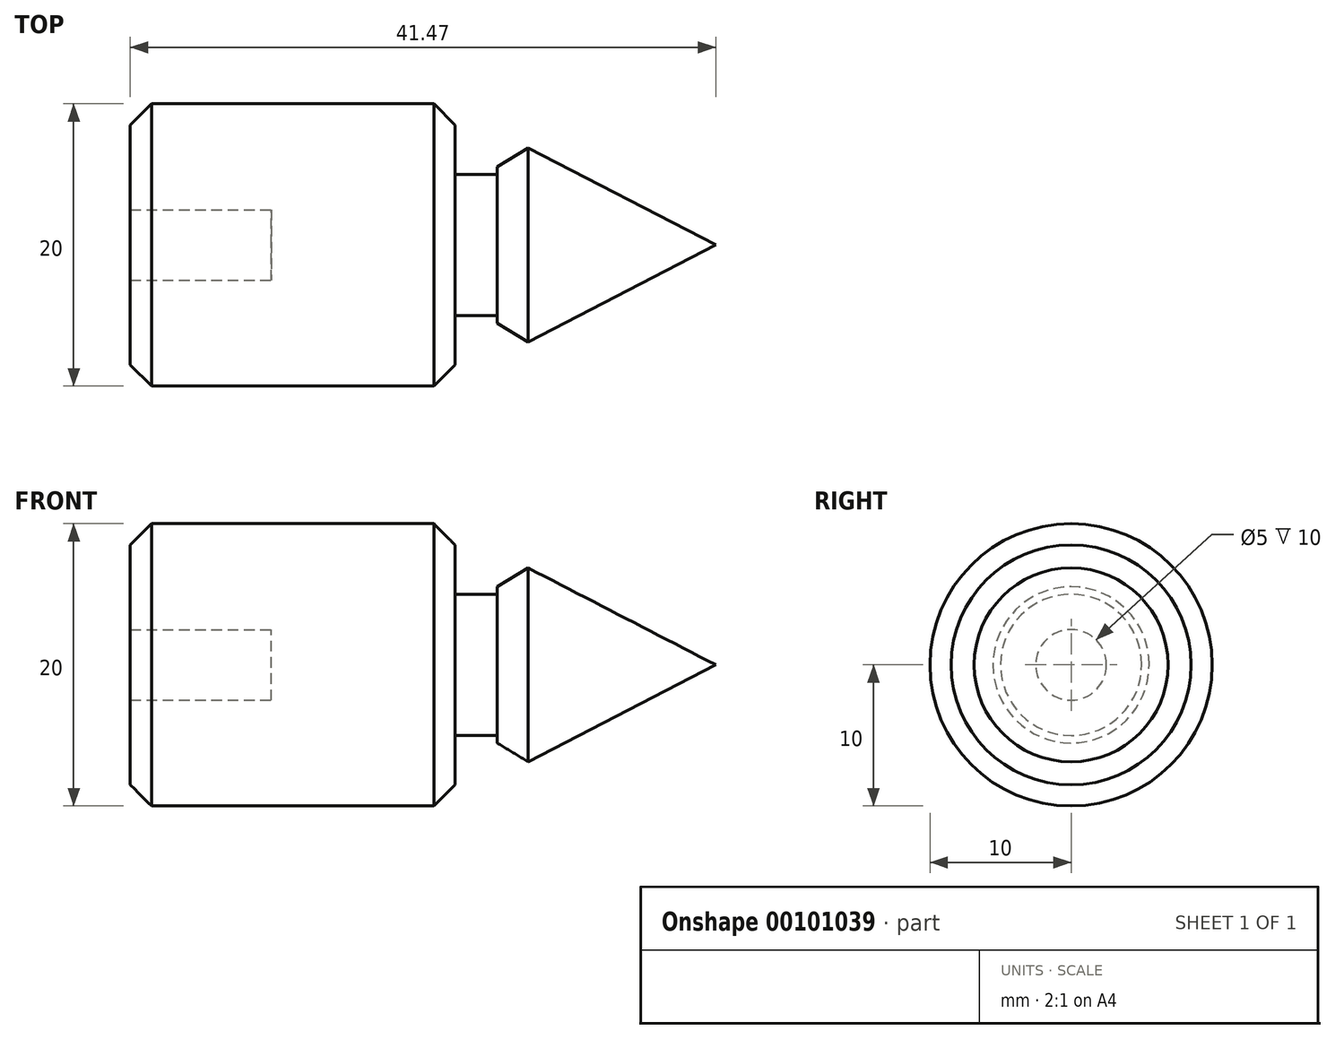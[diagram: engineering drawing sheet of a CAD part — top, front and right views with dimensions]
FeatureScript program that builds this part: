
annotation { "Feature Type Name" : "Feature", "Feature Type Description" : "" }
export const myFeature = defineFeature(function(context is Context, id is Id, definition is map)
    precondition{}
    {
        {
            var Q0;
            Q0=qCreatedBy(makeId("Top.planeOp"),FACE);
            var sketch = newSketch(context, id + "F0", { "sketchPlane" : qUnion([Q0])});
            skLineSegment(sketch, "E0", {"start": v(0, 5) * mm, "end": v(3, 5) * mm});
            skLineSegment(sketch, "E1", {"start": v(3, 5) * mm, "end": v(3, 8) * mm});
            skLineSegment(sketch, "E2", {"start": v(3, 8) * mm, "end": v(18.47, 0) * mm});
            skLineSegment(sketch, "E3", {"start": v(18.47, 0) * mm, "end": v(0, 0) * mm});
            skLineSegment(sketch, "E4", {"start": v(0, 0) * mm, "end": v(-13, 0) * mm});
            skLineSegment(sketch, "E5", {"start": v(-23, 2.5) * mm, "end": v(-23, 10) * mm});
            skLineSegment(sketch, "E6", {"start": v(-23, 10) * mm, "end": v(0, 10) * mm});
            skLineSegment(sketch, "E7", {"start": v(0, 10) * mm, "end": v(0, 5) * mm});
            skLineSegment(sketch, "E8", {"start": v(-23, 2.5) * mm, "end": v(-22, 2.5) * mm});
            skLineSegment(sketch, "E9", {"start": v(-13, 2.5) * mm, "end": v(-13, 0) * mm});
            skLineSegment(sketch, "E10", {"start": v(-23, 2.5) * mm, "end": v(-13, 2.5) * mm});
            skSolve(sketch);
        }
        {
            var Q0;
            Q0=makeQuery(id+"F0.imprint","IMPRINT",FACE,{"disambiguationData":[TD([[makeQuery(id+"F0.imprint","IMPRINT",EDGE,{"derivedFrom":sQuery(id+"F0.wireOp",EDGE,"E0")}),-1.0]])]});
            var Q1;
            Q1=sQuery(id+"F0.wireOp",EDGE,"E3");
            revolve(context, id + "F1", {"entities" : qUnion([Q0]), "axis" : qUnion([Q1]), "revolveType" : RevolveType.FULL});
        }
        {
            var Q0;
            Q0=makeQuery(id+"F1.opRevolve","SWEPT_FACE",FACE,{"disambiguationData":[OSD([sQuery(id+"F0.wireOp",EDGE,"E6")])]});
            chamfer(context, id + "F2", {"entities" : qUnion([Q0]), "width" : 1.5 * mm, "tangentPropagation" : true});
        }
        {
            var Q0;
            Q0=makeQuery(id+"F1.opRevolve","SWEPT_EDGE",EDGE,{"disambiguationData":[OSD([sQuery(id+"F0.wireOp",EDGE,"E1"),sQuery(id+"F0.wireOp",EDGE,"E2")])]});
            chamfer(context, id + "F3", {"entities" : qUnion([Q0]), "width" : 1.5 * mm, "tangentPropagation" : true});
        }
    });
